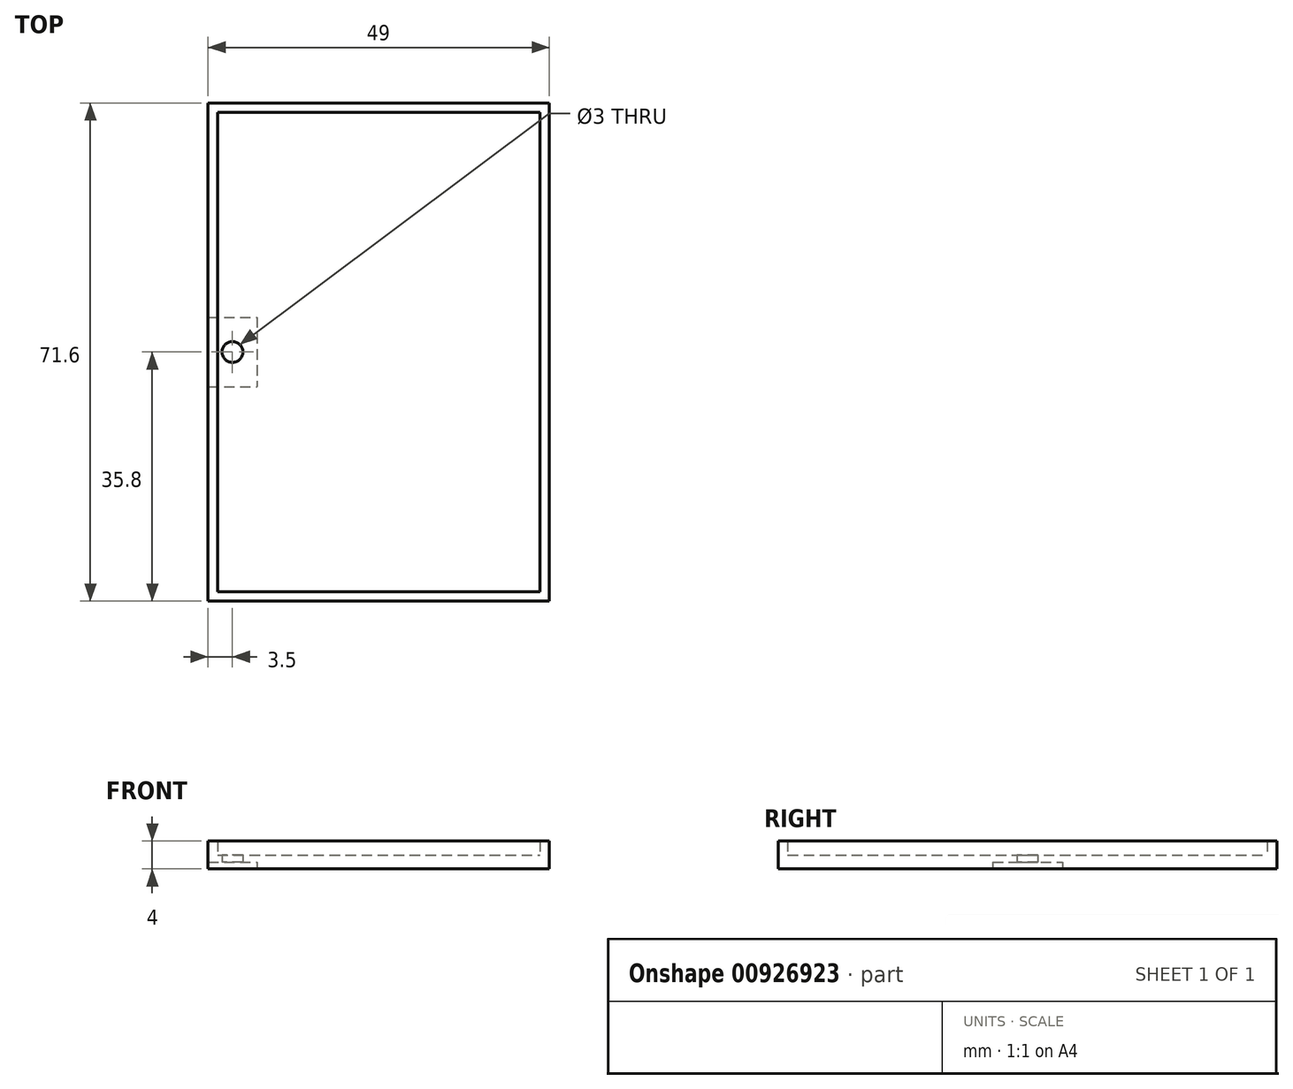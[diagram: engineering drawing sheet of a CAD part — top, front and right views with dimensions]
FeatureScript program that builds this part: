
annotation { "Feature Type Name" : "Feature", "Feature Type Description" : "" }
export const myFeature = defineFeature(function(context is Context, id is Id, definition is map)
    precondition{}
    {
        {
            var Q0;
            Q0=qCreatedBy(makeId("Top.planeOp"),FACE);
            var sketch = newSketch(context, id + "F0", { "sketchPlane" : qUnion([Q0])});
            skLineSegment(sketch, "E0.bottom", {"start": v(-24.5, -35.8) * mm, "end": v(24.5, -35.8) * mm});
            skLineSegment(sketch, "E0.top", {"start": v(-24.5, 35.8) * mm, "end": v(24.5, 35.8) * mm});
            skLineSegment(sketch, "E0.left", {"start": v(-24.5, -35.8) * mm, "end": v(-24.5, 35.8) * mm});
            skLineSegment(sketch, "E0.right", {"start": v(24.5, -35.8) * mm, "end": v(24.5, 35.8) * mm});
            skPoint(sketch, "E0.middle", {"position": v(0, 0) * mm});
            skLineSegment(sketch, "E1.0", {"start": v(-23.15, -34.45) * mm, "end": v(23.15, -34.45) * mm});
            skLineSegment(sketch, "E1.1", {"start": v(-23.15, -34.45) * mm, "end": v(-23.15, 34.45) * mm});
            skLineSegment(sketch, "E1.2", {"start": v(-23.15, 34.45) * mm, "end": v(23.15, 34.45) * mm});
            skLineSegment(sketch, "E1.3", {"start": v(23.15, -34.45) * mm, "end": v(23.15, 34.45) * mm});
            skSolve(sketch);
        }
        {
            var Q0;
            Q0=makeQuery(id+"F0.imprint","IMPRINT",FACE,{"disambiguationData":[TD([[makeQuery(id+"F0.imprint","IMPRINT",EDGE,{"derivedFrom":sQuery(id+"F0.wireOp",EDGE,"E0.bottom")}),1.0]])]});
            extrude(context, id + "F1", {"entities" : qUnion([Q0]), "depth" : 4 * mm, "offsetDistance" : 25 * mm});
        }
        {
            var Q0;
            Q0=makeQuery(id+"F0.imprint","IMPRINT",FACE,{"disambiguationData":[TD([[makeQuery(id+"F0.imprint","IMPRINT",EDGE,{"derivedFrom":sQuery(id+"F0.wireOp",EDGE,"E1.0")}),1.0]])]});
            extrude(context, id + "F2", {"entities" : qUnion([Q0]), "operationType" : NewBodyOperationType.ADD, "depth" : 2 * mm, "offsetDistance" : 25 * mm});
        }
        {
            var Q0;
            Q0=makeQuery(id+"F0.imprint","IMPRINT",FACE,{"disambiguationData":[TD([[makeQuery(id+"F0.imprint","IMPRINT",EDGE,{"derivedFrom":sQuery(id+"F0.wireOp",EDGE,"E0.bottom")}),1.0]])]});
            var sketch = newSketch(context, id + "F3", { "sketchPlane" : qUnion([Q0])});
            skLineSegment(sketch, "E2", {"start": v(-24.5, -5) * mm, "end": v(-17.5, -5) * mm});
            skLineSegment(sketch, "E3", {"start": v(-24.5, 5) * mm, "end": v(-24.5, -5) * mm});
            skLineSegment(sketch, "E4", {"start": v(-17.5, 5) * mm, "end": v(-17.5, -5) * mm});
            skLineSegment(sketch, "E5", {"start": v(-24.5, 5) * mm, "end": v(-17.5, 5) * mm});
            skCircle(sketch, "E6", {"center": v(-21, 0) * mm, "radius": 1.5 * mm});
            skPoint(sketch, "E6.centerSnap0", {"position": v(-21, -5) * mm});
            skPoint(sketch, "E6.centerSnap1", {"position": v(-17.5, 0) * mm});
            skSolve(sketch);
        }
        {
            var Q0;
            {var subQ0=sQuery(id+"F3.wireOp",EDGE,"E4");Q0=makeQuery(id+"F3.imprint","IMPRINT",FACE,{"disambiguationData":[TD([[makeQuery(id+"F3.imprint","IMPRINT",EDGE,{"derivedFrom":subQ0}),-1.0]])]});}
            var Q1;
            {var subQ0=sQuery(id+"F3.wireOp",EDGE,"E3");Q1=makeQuery(id+"F3.imprint","IMPRINT",FACE,{"disambiguationData":[TD([[makeQuery(id+"F3.imprint","IMPRINT",EDGE,{"derivedFrom":subQ0}),-1.0]])]});}
            extrude(context, id + "F4", {"entities" : qUnion([Q0, Q1]), "operationType" : NewBodyOperationType.REMOVE, "depth" : 1 * mm, "offsetDistance" : 25 * mm});
        }
        {
            var Q0;
            Q0=makeQuery(id+"F3.imprint","IMPRINT",FACE,{"disambiguationData":[TD([[makeQuery(id+"F3.imprint","IMPRINT",EDGE,{"derivedFrom":sQuery(id+"F3.wireOp",EDGE,"E6")}),1.0]])]});
            extrude(context, id + "F5", {"entities" : qUnion([Q0]), "operationType" : NewBodyOperationType.REMOVE, "depth" : 4.9 * mm, "offsetDistance" : 25 * mm});
        }
    });
